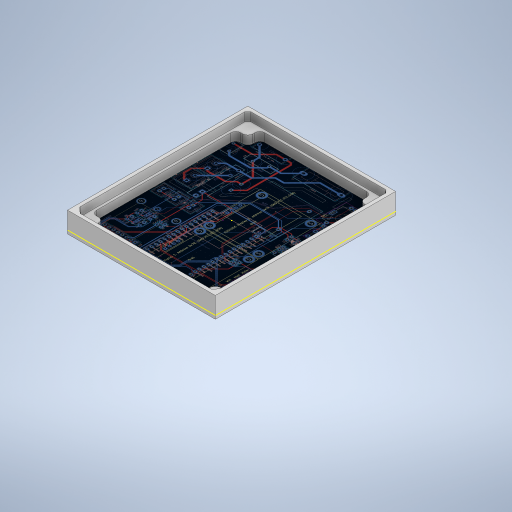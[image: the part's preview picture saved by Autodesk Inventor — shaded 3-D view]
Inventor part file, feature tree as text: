
AUTODESK INVENTOR PART (.ipt)
format: ipt  version: 2024 (Build 280153000, 153)  size: 1,273,856 bytes
history: native  units: mm
features: sketch x4, extrude x3, other x2, projected_geometry x2, fillet x1
ambient origin geometry x8: Origin, YZ Plane, XZ Plane, XY Plane, X Axis, Y Axis, Z Axis, Center Point
bodies: Body1 (feature_tree)
feature tree (12):
  extrude  "Extrusion3"  Depth=100.9mm
  extrude  "Extrusion4"  Depth=104.9mm
  sketch  "Sketch4"  dims[d102=10.0mm d103=0.0mm d104=2.0mm d105=0.0mm d150=5.0mm d151=0.0mm]
  extrude  "Extrusion5"  Depth=2.0mm TaperAngle=0.0deg
  fillet  "Fillet1"  Radius=5.0mm
  sketch  "Sketch1"  dims[d48=82.0mm d49=100.9mm]
  other  "Image2"
  sketch  "Sketch3"  dims[d50=86.0mm d51=104.9mm]
  other  "Image3"
  projected_geometry  "Projected Loop1"
  sketch  "Sketch5"  dims[d152=7.0mm d153=7.0mm d154=7.0mm d155=7.0mm d156=7.0mm d157=7.0mm d158=7.0mm d159=7.0mm d160=3.0mm]
  projected_geometry  "Projected Loop2"
